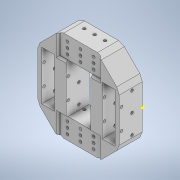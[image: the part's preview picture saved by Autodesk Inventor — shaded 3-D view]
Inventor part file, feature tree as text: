
AUTODESK INVENTOR PART (.ipt)
format: ipt  version: 2022 (Build 260153000, 153)  size: 328,192 bytes
history: native  units: in
note: dims shown in document units (in); Inventor stores cm internally (conversion verified against a paired STEP export)
features: sketch x9, extrude x7, projected_geometry x3, chamfer x2
ambient origin geometry x8: Origin, YZ Plane, XZ Plane, XY Plane, X Axis, Y Axis, Z Axis, Center Point
bodies: Solid1 (feature_tree)
feature tree (21):
  extrude  "Extrusion1"  Depth=1.3189in TaperAngle=0.0deg
  extrude  "Extrusion2"  Depth=0.7283in
  extrude  "Extrusion3"  Depth=0.0787in TaperAngle=0.0deg
  chamfer  "Chamfer1"  Distance=0.125in
  chamfer  "Chamfer2"  Distance=0.0787in Angle=45.0deg
  extrude  "Extrusion4"  Depth=0.0787in
  extrude  "Extrusion5"  Depth=0.1575in
  sketch  "Sketch6"  dims[d35=0.1575in d36=0.1575in]
  extrude  "Extrusion6"  Depth=0.1575in
  sketch  "Sketch8"  dims[d39=0.1575in]
  extrude  "Extrusion7"  Depth=0.1575in
  sketch  "Sketch1"  dims[d2=0.2362in d5=1.3189in d6=0.0in]
  sketch  "Sketch2"  dims[d16=0.7283in d17=2.0866in]
  projected_geometry  "Projected Loop1"
  sketch  "Sketch3"  dims[d18=2.0866in d20=0.1083in d21=0.0in d22=0.125in d23=0.0in d24=0.1969in d25=0.0787in d26=45.0deg]
  sketch  "Sketch4"  dims[d27=0.0984in d28=0.0787in d29=45.0deg d30=0.315in]
  sketch  "Sketch5"  dims[d31=0.315in d34=0.1575in]
  sketch  "Sketch7"  dims[d37=0.1575in d38=0.1575in]
  sketch  "Sketch9"  dims[d40=0.0in d41=0.0in d48=0.0in d49=0.0in d50=0.3937in d51=0.5906in d52=1.1811in d53=0.1575in d54=0.1575in d55=0.1575in d56=0.0in d57=0.0in d58=0.1575in d61=0.3937in d62=0.0in]
  projected_geometry  "Projected Loop2"
  projected_geometry  "Projected Loop3"
